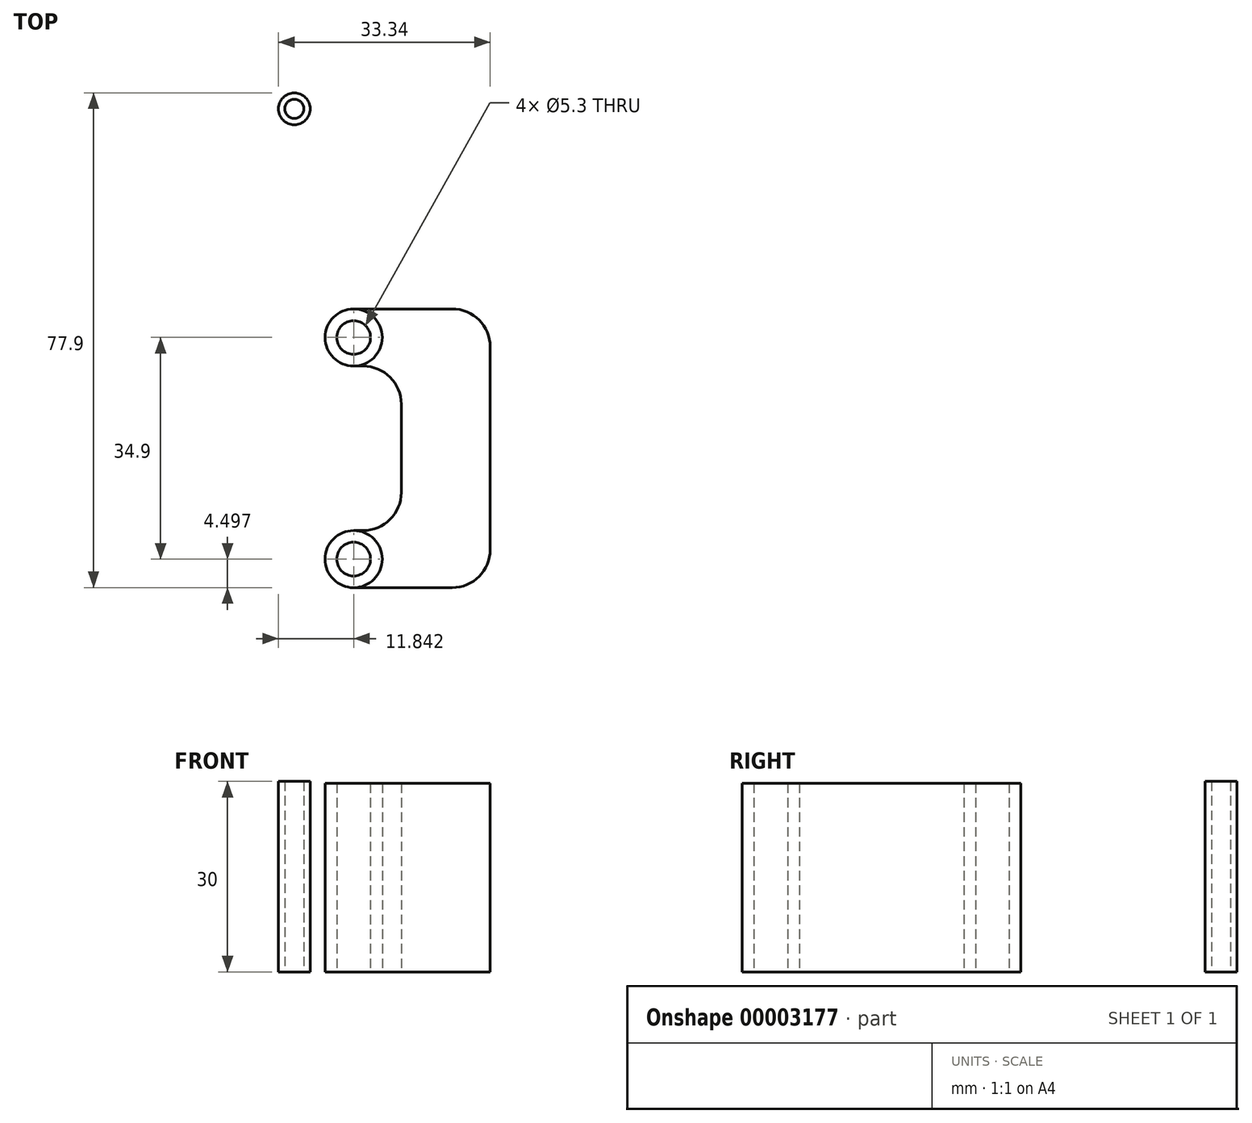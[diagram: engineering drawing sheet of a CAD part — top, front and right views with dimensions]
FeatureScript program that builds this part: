
annotation { "Feature Type Name" : "Feature", "Feature Type Description" : "" }
export const myFeature = defineFeature(function(context is Context, id is Id, definition is map)
    precondition{}
    {
        {
            var Q0;
            Q0=qCreatedBy(makeId("Top.planeOp"),FACE);
            var sketch = newSketch(context, id + "F0", { "sketchPlane" : qUnion([Q0])});
            skCircle(sketch, "E0", {"center": v(-43.24, 23.2) * mm, "radius": 2.5 * mm});
            skCircle(sketch, "E1", {"center": v(-43.24, 23.2) * mm, "radius": 1.5 * mm});
            skSolve(sketch);
        }
        {
            var Q0;
            Q0 = qSketchRegion(id + "F0", true);
            extrude(context, id + "F1", {"entities" : qUnion([Q0]), "depth" : 30 * mm});
        }
        {
            var Q0;
            Q0=qCreatedBy(makeId("Top.planeOp"),FACE);
            var sketch = newSketch(context, id + "F2", { "sketchPlane" : qUnion([Q0])});
            skCircle(sketch, "E2", {"center": v(-33.9, -47.7) * mm, "radius": 4.5 * mm});
            skCircle(sketch, "E3", {"center": v(-33.9, -47.7) * mm, "radius": 2.65 * mm});
            skCircle(sketch, "E4", {"center": v(-33.9, -12.8) * mm, "radius": 4.5 * mm});
            skCircle(sketch, "E5", {"center": v(-33.9, -12.8) * mm, "radius": 2.65 * mm});
            skSolve(sketch);
        }
        {
            var Q0;
            Q0 = qSketchRegion(id + "F2", true);
            extrude(context, id + "F3", {"entities" : qUnion([Q0]), "depth" : 29.7 * mm});
        }
        {
            var Q0;
            Q0=makeQuery(id+"F3.opExtrude","CAP_FACE",FACE,{"disambiguationData":[OSD([sQuery(id+"F2.wireOp",EDGE,"E4"),sQuery(id+"F2.wireOp",EDGE,"E5")])],"isStart":true});
            var sketch = newSketch(context, id + "F4", { "sketchPlane" : qUnion([Q0])});
            skLineSegment(sketch, "E6", {"start": v(-33.9, 8.3) * mm, "end": v(-18.4, 8.3) * mm});
            skLineSegment(sketch, "E7", {"start": v(-12.4, 14.3) * mm, "end": v(-12.4, 46.2) * mm});
            skLineSegment(sketch, "E8", {"start": v(-18.4, 52.2) * mm, "end": v(-33.9, 52.2) * mm});
            skLineSegment(sketch, "E9", {"start": v(-33.9, 17.3) * mm, "end": v(-32.4, 17.3) * mm});
            skLineSegment(sketch, "E10", {"start": v(-26.4, 23.3) * mm, "end": v(-26.4, 37.2) * mm});
            skLineSegment(sketch, "E11", {"start": v(-32.4, 43.2) * mm, "end": v(-33.9, 43.2) * mm});
            skPoint(sketch, "E12.visualSharp", {"position": v(-26.4, 17.3) * mm});
            skArc(sketch, "E12.filletArc", {"start": v(-32.4, 17.3) * mm, "mid": v(-28.16, 19.05) * mm, "end": v(-26.4, 23.3) * mm});
            skPoint(sketch, "E13.visualSharp", {"position": v(-26.4, 43.2) * mm});
            skArc(sketch, "E13.filletArc", {"start": v(-26.4, 37.2) * mm, "mid": v(-28.16, 41.44) * mm, "end": v(-32.4, 43.2) * mm});
            skPoint(sketch, "E14.visualSharp", {"position": v(-12.4, 8.3) * mm});
            skArc(sketch, "E14.filletArc", {"start": v(-18.4, 8.3) * mm, "mid": v(-14.16, 10.05) * mm, "end": v(-12.4, 14.3) * mm});
            skPoint(sketch, "E15.visualSharp", {"position": v(-12.4, 52.2) * mm});
            skArc(sketch, "E15.filletArc", {"start": v(-12.4, 46.2) * mm, "mid": v(-14.16, 50.44) * mm, "end": v(-18.4, 52.2) * mm});
            skCircle(sketch, "E16", {"center": v(-33.9, 12.8) * mm, "radius": 4.5 * mm});
            skCircle(sketch, "E17", {"center": v(-33.9, 47.7) * mm, "radius": 4.5 * mm});
            skCircle(sketch, "E18", {"center": v(-33.9, 12.8) * mm, "radius": 2.65 * mm});
            skCircle(sketch, "E19", {"center": v(-33.9, 47.7) * mm, "radius": 2.65 * mm});
            skSolve(sketch);
        }
        {
            var Q0;
            Q0 = qSketchRegion(id + "F4", true);
            extrude(context, id + "F5", {"entities" : qUnion([Q0]), "oppositeDirection" : true, "depth" : 29.7 * mm});
        }
    });
